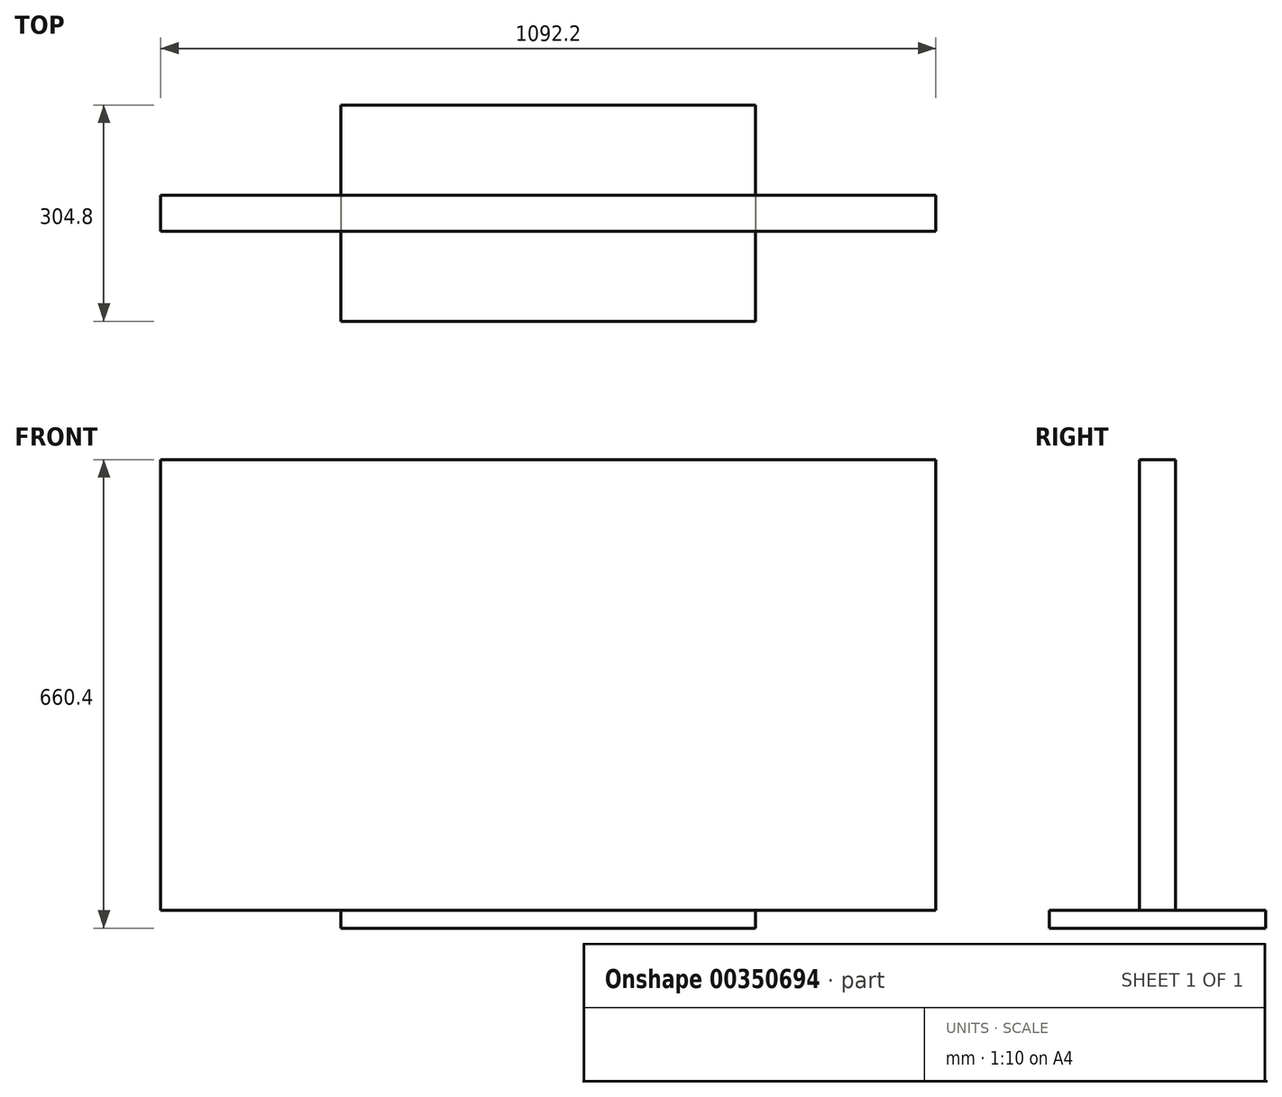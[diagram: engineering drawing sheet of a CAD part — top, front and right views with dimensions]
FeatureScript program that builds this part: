
annotation { "Feature Type Name" : "Feature", "Feature Type Description" : "" }
export const myFeature = defineFeature(function(context is Context, id is Id, definition is map)
    precondition{}
    {
        {
            var Q0;
            Q0=qCreatedBy(makeId("Top.planeOp"),FACE);
            var sketch = newSketch(context, id + "F0", { "sketchPlane" : qUnion([Q0])});
            skLineSegment(sketch, "E0.bottom", {"start": v(-292.1, 152.4) * mm, "end": v(292.1, 152.4) * mm});
            skLineSegment(sketch, "E0.top", {"start": v(-292.1, -152.4) * mm, "end": v(292.1, -152.4) * mm});
            skLineSegment(sketch, "E0.left", {"start": v(-292.1, 152.4) * mm, "end": v(-292.1, -152.4) * mm});
            skLineSegment(sketch, "E0.right", {"start": v(292.1, 152.4) * mm, "end": v(292.1, -152.4) * mm});
            skPoint(sketch, "E0.middle", {"position": v(0, 0) * mm});
            skSolve(sketch);
        }
        {
            var Q0;
            Q0=makeQuery(id+"F0.imprint","IMPRINT",FACE,{"disambiguationData":[TD([[makeQuery(id+"F0.imprint","IMPRINT",EDGE,{"derivedFrom":sQuery(id+"F0.wireOp",EDGE,"E0.bottom")}),-1.0]])]});
            extrude(context, id + "F1", {"entities" : qUnion([Q0]), "depth" : 25.4 * mm});
        }
        {
            var Q0;
            Q0=makeQuery(id+"F1.opExtrude","CAP_FACE",FACE,{"disambiguationData":[OSD([sQuery(id+"F0.wireOp",EDGE,"E0.bottom"),sQuery(id+"F0.wireOp",EDGE,"E0.top"),sQuery(id+"F0.wireOp",EDGE,"E0.left"),sQuery(id+"F0.wireOp",EDGE,"E0.right")])],"isStart":false});
            var sketch = newSketch(context, id + "F2", { "sketchPlane" : qUnion([Q0])});
            skLineSegment(sketch, "E1.bottom", {"start": v(-546.1, -25.4) * mm, "end": v(546.1, -25.4) * mm});
            skLineSegment(sketch, "E1.top", {"start": v(-546.1, 25.4) * mm, "end": v(546.1, 25.4) * mm});
            skLineSegment(sketch, "E1.left", {"start": v(-546.1, -25.4) * mm, "end": v(-546.1, 25.4) * mm});
            skLineSegment(sketch, "E1.right", {"start": v(546.1, -25.4) * mm, "end": v(546.1, 25.4) * mm});
            skPoint(sketch, "E1.middle", {"position": v(0, 0) * mm});
            skSolve(sketch);
        }
        {
            var Q0;
            {var subQ0=sQuery(id+"F2.wireOp",EDGE,"E1.left");Q0=makeQuery(id+"F2.imprint","IMPRINT",FACE,{"disambiguationData":[TD([[makeQuery(id+"F2.imprint","IMPRINT",EDGE,{"derivedFrom":subQ0}),-1.0]])]});}
            var Q1;
            {var subQ0=sQuery(id+"F2.wireOp",EDGE,"E1.bottom");var subQ1=makeQuery(id+"F1.opExtrude","CAP_EDGE",EDGE,{"disambiguationData":[OSD([sQuery(id+"F0.wireOp",EDGE,"E0.left")])],"isStart":false});var subQ2=makeQuery(id+"F2.imprint","INTERSECT",VERTEX,{"derivedFrom":[subQ1,subQ0]});Q1=makeQuery(id+"F2.imprint","IMPRINT",FACE,{"disambiguationData":[TD([[makeQuery(id+"F2.imprint","IMPRINT",EDGE,{"disambiguationData":[TD([[subQ2,-1.0]])],"derivedFrom":subQ0}),1.0]])]});}
            var Q2;
            {var subQ0=sQuery(id+"F2.wireOp",EDGE,"E1.right");Q2=makeQuery(id+"F2.imprint","IMPRINT",FACE,{"disambiguationData":[TD([[makeQuery(id+"F2.imprint","IMPRINT",EDGE,{"derivedFrom":subQ0}),1.0]])]});}
            extrude(context, id + "F3", {"entities" : qUnion([Q0, Q1, Q2]), "operationType" : NewBodyOperationType.ADD, "depth" : 635 * mm});
        }
    });
